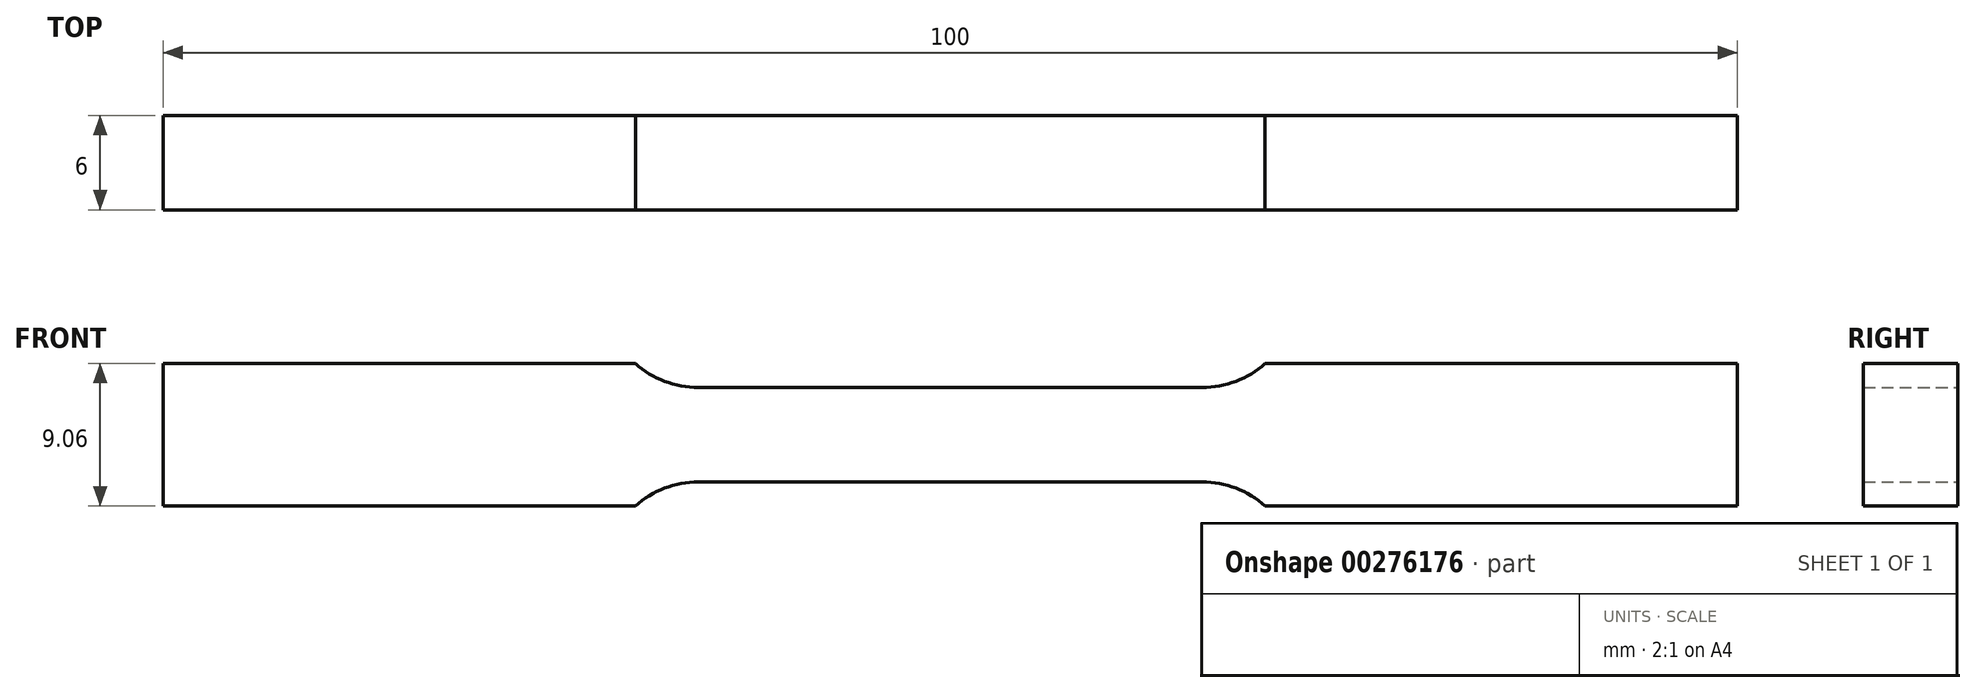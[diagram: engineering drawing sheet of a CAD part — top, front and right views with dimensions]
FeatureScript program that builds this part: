
annotation { "Feature Type Name" : "Feature", "Feature Type Description" : "" }
export const myFeature = defineFeature(function(context is Context, id is Id, definition is map)
    precondition{}
    {
        {
            var Q0;
            Q0=qCreatedBy(makeId("Front.planeOp"),FACE);
            var sketch = newSketch(context, id + "F0", { "sketchPlane" : qUnion([Q0])});
            skLineSegment(sketch, "E0", {"start": v(0, 3) * mm, "end": v(16, 3) * mm});
            skArc(sketch, "E1", {"start": v(16, 3) * mm, "mid": v(18.14, 3.4) * mm, "end": v(20, 4.53) * mm});
            skLineSegment(sketch, "E2", {"start": v(20, 4.53) * mm, "end": v(50, 4.53) * mm});
            skLineSegment(sketch, "E3", {"start": v(50, 4.53) * mm, "end": v(50, 0) * mm});
            skLineSegment(sketch, "E4.MirrorCS", {"start": v(50, -4.53) * mm, "end": v(50, 0) * mm});
            skArc(sketch, "E5.MirrorCS", {"start": v(16, -3) * mm, "mid": v(18.14, -3.4) * mm, "end": v(20, -4.53) * mm});
            skLineSegment(sketch, "E6.MirrorCS", {"start": v(0, -3) * mm, "end": v(16, -3) * mm});
            skLineSegment(sketch, "E7.MirrorCS", {"start": v(20, -4.53) * mm, "end": v(50, -4.53) * mm});
            skLineSegment(sketch, "E8.MirrorCS", {"start": v(-50, 4.53) * mm, "end": v(-50, 0) * mm});
            skLineSegment(sketch, "E9.MirrorCS", {"start": v(0, 3) * mm, "end": v(-16, 3) * mm});
            skLineSegment(sketch, "E10.MirrorCS", {"start": v(-50, -4.53) * mm, "end": v(-50, 0) * mm});
            skArc(sketch, "E11.MirrorCS", {"start": v(-16, -3) * mm, "mid": v(-18.14, -3.4) * mm, "end": v(-20, -4.53) * mm});
            skLineSegment(sketch, "E12.MirrorCS", {"start": v(-20, 4.53) * mm, "end": v(-50, 4.53) * mm});
            skArc(sketch, "E13.MirrorCS", {"start": v(-16, 3) * mm, "mid": v(-18.14, 3.4) * mm, "end": v(-20, 4.53) * mm});
            skLineSegment(sketch, "E14.MirrorCS", {"start": v(-20, -4.53) * mm, "end": v(-50, -4.53) * mm});
            skLineSegment(sketch, "E15.MirrorCS", {"start": v(0, -3) * mm, "end": v(-16, -3) * mm});
            skSolve(sketch);
        }
        {
            var Q0;
            Q0 = qSketchRegion(id + "F0", true);
            extrude(context, id + "F1", {"entities" : qUnion([Q0]), "endBound" : BoundingType.SYMMETRIC, "depth" : 6 * mm});
        }
    });
